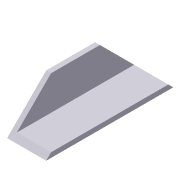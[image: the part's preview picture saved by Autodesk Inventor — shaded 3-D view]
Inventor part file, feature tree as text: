
AUTODESK INVENTOR PART (.ipt)
format: ipt  version: 2012 (Build 160160000, 160)  size: 69,632 bytes
history: native  units: in
note: dims shown in document units (in); Inventor stores cm internally (conversion verified against a paired STEP export)
features: extrude x1, chamfer x1, sketch x1
ambient origin geometry x8: Origin, YZ Plane, XZ Plane, XY Plane, X Axis, Y Axis, Z Axis, Center Point
bodies: Solid1 (feature_tree)
feature tree (3):
  extrude  "Extrusion1"  Depth=0.125in
  chamfer  "Chamfer1"  Distance=3.25in
  sketch  "Sketch1"  dims[d0=1.0in d1=0.125in d2=3.25in d3=0.0in d4=1.0in d5=0.125in d6=45.0deg]
